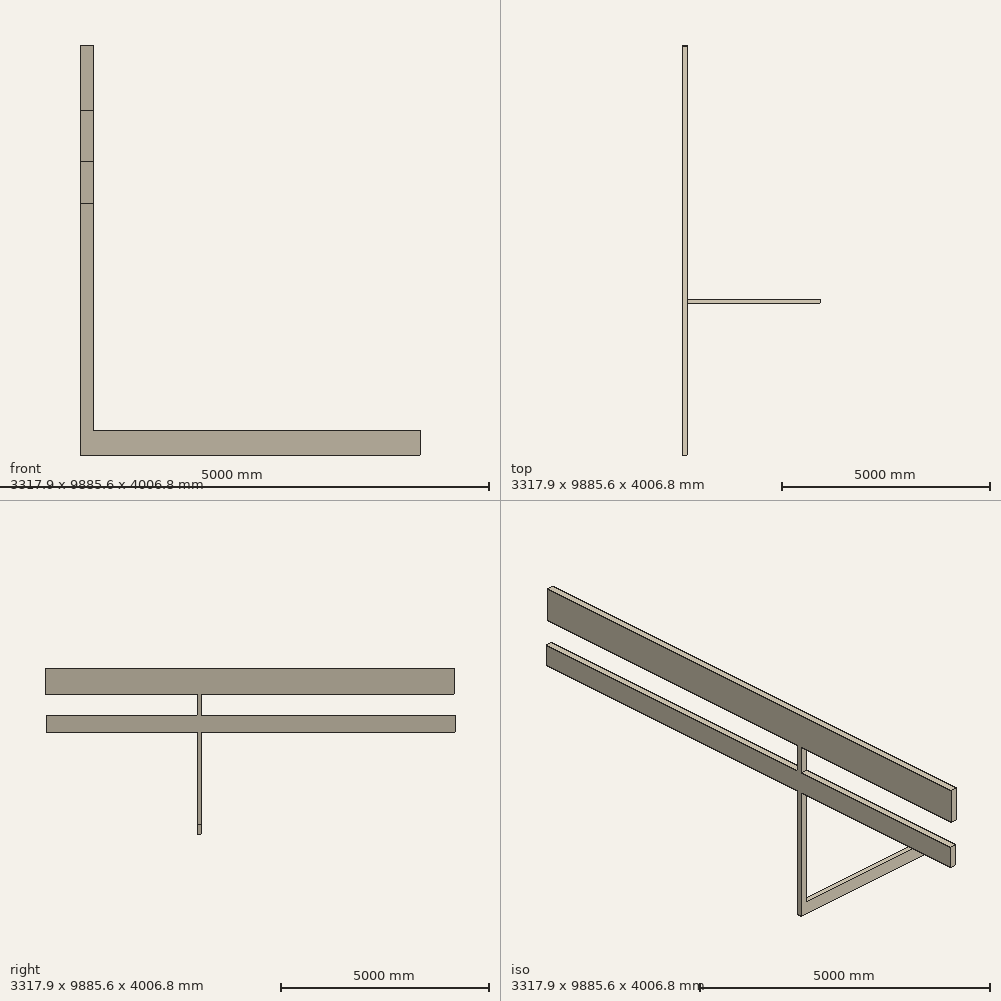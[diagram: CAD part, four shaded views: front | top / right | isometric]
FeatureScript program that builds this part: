
annotation { "Feature Type Name" : "Feature", "Feature Type Description" : "" }
export const myFeature = defineFeature(function(context is Context, id is Id, definition is map)
    precondition{}
    {
        {
            var Q0;
            Q0=qCreatedBy(makeId("Right.planeOp"),FACE);
            var sketch = newSketch(context, id + "F0", { "sketchPlane" : qUnion([Q0])});
            skLineSegment(sketch, "E0.bottom", {"start": v(50.8, 1882.78) * mm, "end": v(-50.8, 1882.78) * mm});
            skLineSegment(sketch, "E0.top", {"start": v(50.8, -1882.78) * mm, "end": v(-50.8, -1882.78) * mm});
            skLineSegment(sketch, "E0.left", {"start": v(50.8, 1882.78) * mm, "end": v(50.8, -1882.78) * mm});
            skLineSegment(sketch, "E0.right", {"start": v(-50.8, 1882.78) * mm, "end": v(-50.8, -1882.78) * mm});
            skPoint(sketch, "E0.middle", {"position": v(0, 0) * mm});
            skLineSegment(sketch, "E1.bottom", {"start": v(-50.8, 1882.78) * mm, "end": v(6146.8, 1882.78) * mm});
            skLineSegment(sketch, "E1.top", {"start": v(-50.8, 1247.78) * mm, "end": v(6146.8, 1247.78) * mm});
            skLineSegment(sketch, "E1.left", {"start": v(-50.8, 1882.78) * mm, "end": v(-50.8, 1247.78) * mm});
            skLineSegment(sketch, "E1.right", {"start": v(6146.8, 1882.78) * mm, "end": v(6146.8, 1247.77) * mm});
            skLineSegment(sketch, "E2.bottom", {"start": v(-50.8, 1882.78) * mm, "end": v(-3708.4, 1882.78) * mm});
            skLineSegment(sketch, "E2.top", {"start": v(-50.8, 1247.78) * mm, "end": v(-3708.4, 1247.77) * mm});
            skLineSegment(sketch, "E2.right", {"start": v(-3708.4, 1882.77) * mm, "end": v(-3708.4, 1247.77) * mm});
            skLineSegment(sketch, "E3.bottom", {"start": v(-3694.5, 339.72) * mm, "end": v(6177.18, 339.72) * mm});
            skLineSegment(sketch, "E3.top", {"start": v(-3694.5, 746.13) * mm, "end": v(6177.18, 746.13) * mm});
            skLineSegment(sketch, "E3.left", {"start": v(-3694.5, 339.72) * mm, "end": v(-3694.5, 746.13) * mm});
            skLineSegment(sketch, "E3.right", {"start": v(6177.18, 339.72) * mm, "end": v(6177.18, 746.13) * mm});
            skLineSegment(sketch, "E4.top", {"start": v(50.8, -2124.08) * mm, "end": v(-50.8, -2124.08) * mm});
            skLineSegment(sketch, "E4.left", {"start": v(50.8, -1882.78) * mm, "end": v(50.8, -2124.08) * mm});
            skLineSegment(sketch, "E4.right", {"start": v(-50.8, -1882.78) * mm, "end": v(-50.8, -2124.08) * mm});
            skSolve(sketch);
        }
        {
            var Q0;
            Q0=qSketchRegion(id+"F0",true);
            extrude(context, id + "F1", {"entities" : qUnion([Q0]), "endBound" : BoundingType.SYMMETRIC, "depth" : 127 * mm, "offsetDistance" : 25.4 * mm});
        }
        {
            var Q0;
            Q0=makeQuery(id+"F0.imprint","IMPRINT",FACE,{"disambiguationData":[TD([[makeQuery(id+"F0.imprint","IMPRINT",EDGE,{"derivedFrom":sQuery(id+"F0.wireOp",EDGE,"E0.top")}),1.0]])]});
            extrude(context, id + "F2", {"entities" : qUnion([Q0]), "operationType" : NewBodyOperationType.ADD, "depth" : 3254.38 * mm, "offsetDistance" : 25.4 * mm});
        }
    });
